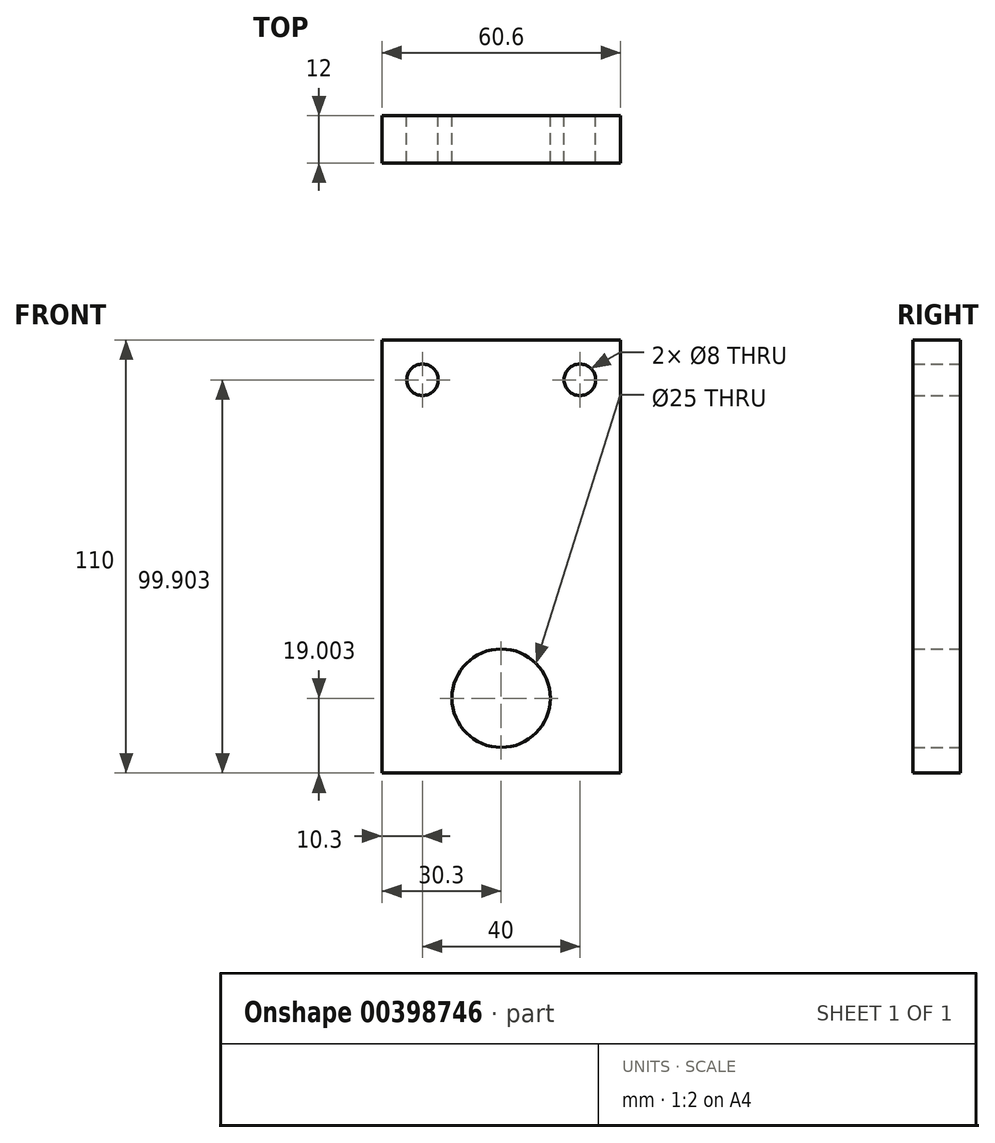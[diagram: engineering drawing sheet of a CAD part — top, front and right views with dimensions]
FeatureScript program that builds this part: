
annotation { "Feature Type Name" : "Feature", "Feature Type Description" : "" }
export const myFeature = defineFeature(function(context is Context, id is Id, definition is map)
    precondition{}
    {
        {
            var Q0;
            Q0=qCreatedBy(makeId("Front.planeOp"),FACE);
            var sketch = newSketch(context, id + "F0", { "sketchPlane" : qUnion([Q0])});
            skLineSegment(sketch, "E0.bottom", {"start": v(-29.56, 66.65) * mm, "end": v(31.04, 66.65) * mm});
            skLineSegment(sketch, "E0.top", {"start": v(-29.56, -43.35) * mm, "end": v(31.04, -43.35) * mm});
            skLineSegment(sketch, "E0.left", {"start": v(-29.56, 66.65) * mm, "end": v(-29.56, -43.35) * mm});
            skLineSegment(sketch, "E0.right", {"start": v(31.04, 66.65) * mm, "end": v(31.04, -43.35) * mm});
            skCircle(sketch, "E1", {"center": v(-19.26, 56.55) * mm, "radius": 4 * mm});
            skCircle(sketch, "E2", {"center": v(20.74, 56.55) * mm, "radius": 4 * mm});
            skCircle(sketch, "E3", {"center": v(0.74, -24.35) * mm, "radius": 12.5 * mm});
            skSolve(sketch);
        }
        {
            var Q0;
            Q0 = qSketchRegion(id + "F0", true);
            extrude(context, id + "F1", {"entities" : qUnion([Q0]), "depth" : 12 * mm});
        }
    });
